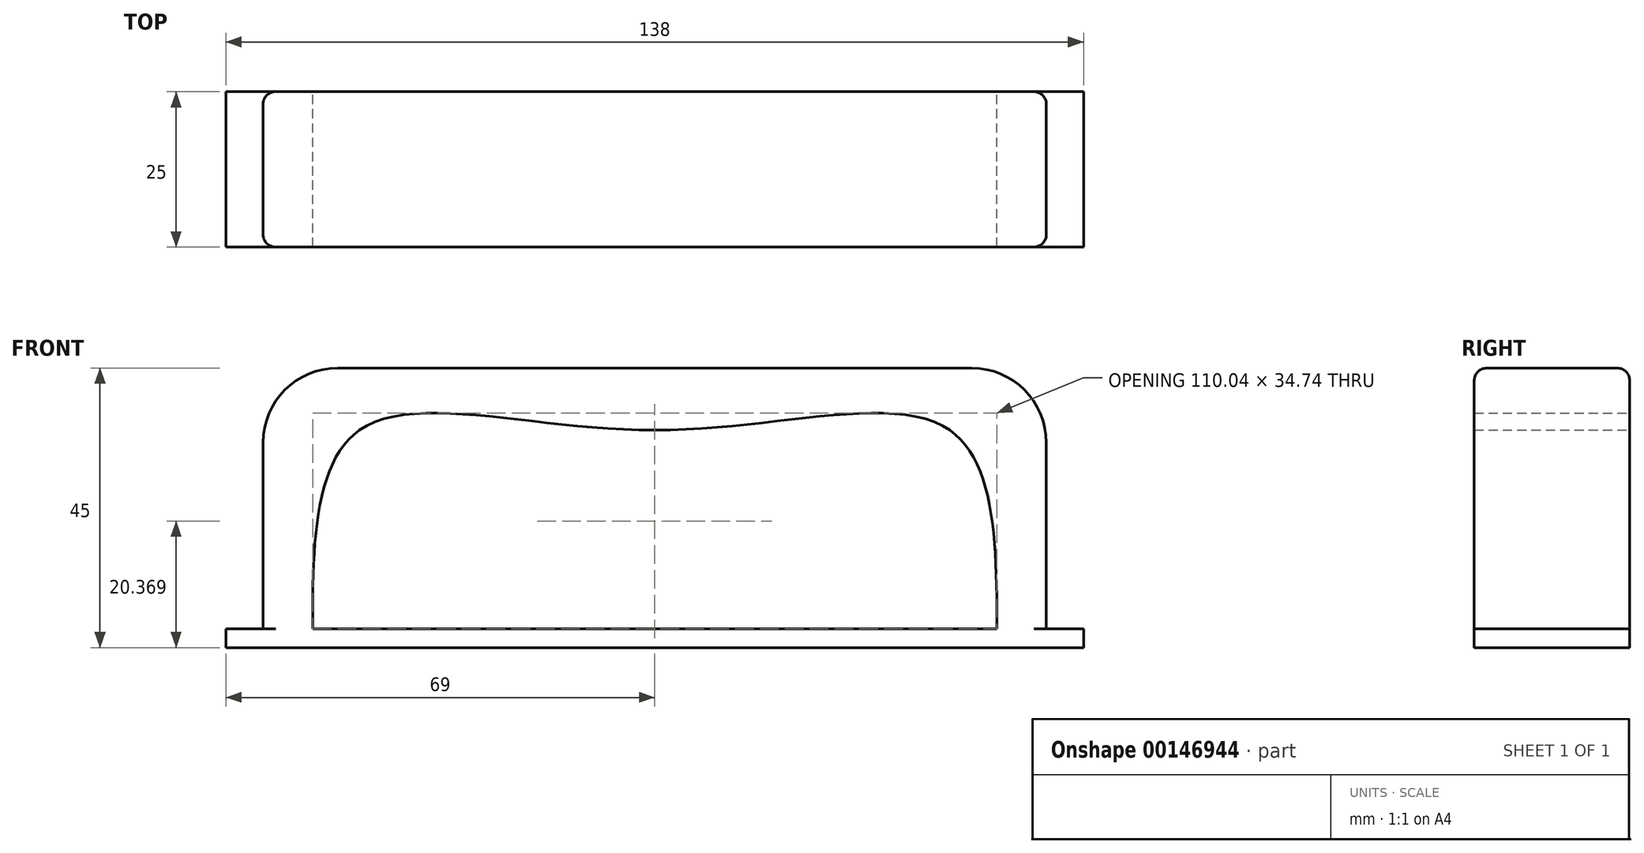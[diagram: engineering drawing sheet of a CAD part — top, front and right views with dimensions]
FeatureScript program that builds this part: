
annotation { "Feature Type Name" : "Feature", "Feature Type Description" : "" }
export const myFeature = defineFeature(function(context is Context, id is Id, definition is map)
    precondition{}
    {
        {
            var Q0;
            Q0=qCreatedBy(makeId("Front.planeOp"),FACE);
            var sketch = newSketch(context, id + "F0", { "sketchPlane" : qUnion([Q0])});
            skLineSegment(sketch, "E0", {"start": v(-55, 0) * mm, "end": v(55, 0) * mm});
            skLineSegment(sketch, "E1", {"start": v(0, 0) * mm, "end": v(0, 35) * mm, "construction": true});
            skLineSegment(sketch, "E2", {"start": v(-47.5, 35) * mm, "end": v(47.5, 35) * mm});
            skFitSpline(sketch, "E3", {"points": [v(-55, 0) * mm, v(-47.5, 35) * mm, v(0, 35) * mm, v(47.5, 35) * mm, v(55, 0) * mm], "startDerivative": vector(-1.45, 191.05) * mm, "endDerivative": vector(-1.45, -191.05) * mm});
            skLineSegment(sketch, "E4", {"start": v(-55, 0) * mm, "end": v(-63, 0) * mm});
            skLineSegment(sketch, "E5", {"start": v(-63, 0) * mm, "end": v(-63, 45) * mm});
            skLineSegment(sketch, "E6", {"start": v(-63, 45) * mm, "end": v(63, 45) * mm});
            skLineSegment(sketch, "E7", {"start": v(63, 45) * mm, "end": v(63, 0) * mm});
            skLineSegment(sketch, "E8", {"start": v(63, 0) * mm, "end": v(55, 0) * mm});
            skLineSegment(sketch, "E9", {"start": v(-63, 0) * mm, "end": v(-69, 0) * mm});
            skLineSegment(sketch, "E10", {"start": v(-69, 0) * mm, "end": v(-69, 3) * mm});
            skLineSegment(sketch, "E11", {"start": v(-69, 3) * mm, "end": v(69, 3) * mm});
            skLineSegment(sketch, "E12", {"start": v(69, 3) * mm, "end": v(69, 0) * mm});
            skLineSegment(sketch, "E13", {"start": v(69, 0) * mm, "end": v(63, 0) * mm});
            skSolve(sketch);
        }
        {
            var Q0;
            Q0 = qSketchRegion(id + "F0", true);
            extrude(context, id + "F1", {"entities" : qUnion([Q0]), "depth" : 25 * mm});
        }
        {
            var Q0;
            Q0=makeQuery(id+"F1.opExtrude","SWEPT_EDGE",EDGE,{"disambiguationData":[OSD([sQuery(id+"F0.wireOp",EDGE,"E5"),sQuery(id+"F0.wireOp",EDGE,"E6")])]});
            var Q1;
            Q1=makeQuery(id+"F1.opExtrude","SWEPT_EDGE",EDGE,{"disambiguationData":[OSD([sQuery(id+"F0.wireOp",EDGE,"E6"),sQuery(id+"F0.wireOp",EDGE,"E7")])]});
            fillet(context, id + "F2", {"entities" : qUnion([Q0, Q1]), "radius" : 12 * mm, "tangentPropagation" : true, "allowEdgeOverflow" : false});
        }
        {
            var Q0;
            Q0=makeQuery(id+"F1.opExtrude","CAP_EDGE",EDGE,{"disambiguationData":[OSD([sQuery(id+"F0.wireOp",EDGE,"E6")])],"isStart":true});
            var Q1;
            {var subQ0=sQuery(id+"F0.wireOp",EDGE,"E6");var subQ1=sQuery(id+"F0.wireOp",EDGE,"E5");Q1=makeQuery(id+"F2.opFillet","BLEND_EDGE",EDGE,{"blendedFrom":[makeQuery(id+"F1.opExtrude","SWEPT_EDGE",EDGE,{"disambiguationData":[OSD([subQ1,subQ0])]}),makeQuery(id+"F1.opExtrude","CAP_FACE",FACE,{"disambiguationData":[OSD([sQuery(id+"F0.wireOp",EDGE,"E0"),sQuery(id+"F0.wireOp",EDGE,"E3"),sQuery(id+"F0.wireOp",EDGE,"E4"),subQ1,subQ0,sQuery(id+"F0.wireOp",EDGE,"E7"),sQuery(id+"F0.wireOp",EDGE,"E8"),sQuery(id+"F0.wireOp",EDGE,"E9"),sQuery(id+"F0.wireOp",EDGE,"E10"),sQuery(id+"F0.wireOp",EDGE,"E11"),sQuery(id+"F0.wireOp",EDGE,"E12"),sQuery(id+"F0.wireOp",EDGE,"E13")])],"isStart":true})],"blendedInto":[makeQuery(id+"F1.opExtrude","CAP_FACE",FACE,{"disambiguationData":[OSD([sQuery(id+"F0.wireOp",EDGE,"E0"),sQuery(id+"F0.wireOp",EDGE,"E3"),sQuery(id+"F0.wireOp",EDGE,"E4"),subQ1,subQ0,sQuery(id+"F0.wireOp",EDGE,"E7"),sQuery(id+"F0.wireOp",EDGE,"E8"),sQuery(id+"F0.wireOp",EDGE,"E9"),sQuery(id+"F0.wireOp",EDGE,"E10"),sQuery(id+"F0.wireOp",EDGE,"E11"),sQuery(id+"F0.wireOp",EDGE,"E12"),sQuery(id+"F0.wireOp",EDGE,"E13")])],"isStart":true})]});}
            var Q2;
            Q2=makeQuery(id+"F1.opExtrude","CAP_EDGE",EDGE,{"disambiguationData":[OSD([sQuery(id+"F0.wireOp",EDGE,"E5")])],"isStart":true});
            var Q3;
            {var subQ0=sQuery(id+"F0.wireOp",EDGE,"E7");var subQ1=sQuery(id+"F0.wireOp",EDGE,"E6");Q3=makeQuery(id+"F2.opFillet","BLEND_EDGE",EDGE,{"blendedFrom":[makeQuery(id+"F1.opExtrude","SWEPT_EDGE",EDGE,{"disambiguationData":[OSD([subQ1,subQ0])]}),makeQuery(id+"F1.opExtrude","CAP_FACE",FACE,{"disambiguationData":[OSD([sQuery(id+"F0.wireOp",EDGE,"E0"),sQuery(id+"F0.wireOp",EDGE,"E3"),sQuery(id+"F0.wireOp",EDGE,"E4"),sQuery(id+"F0.wireOp",EDGE,"E5"),subQ1,subQ0,sQuery(id+"F0.wireOp",EDGE,"E8"),sQuery(id+"F0.wireOp",EDGE,"E9"),sQuery(id+"F0.wireOp",EDGE,"E10"),sQuery(id+"F0.wireOp",EDGE,"E11"),sQuery(id+"F0.wireOp",EDGE,"E12"),sQuery(id+"F0.wireOp",EDGE,"E13")])],"isStart":true})],"blendedInto":[makeQuery(id+"F1.opExtrude","CAP_FACE",FACE,{"disambiguationData":[OSD([sQuery(id+"F0.wireOp",EDGE,"E0"),sQuery(id+"F0.wireOp",EDGE,"E3"),sQuery(id+"F0.wireOp",EDGE,"E4"),sQuery(id+"F0.wireOp",EDGE,"E5"),subQ1,subQ0,sQuery(id+"F0.wireOp",EDGE,"E8"),sQuery(id+"F0.wireOp",EDGE,"E9"),sQuery(id+"F0.wireOp",EDGE,"E10"),sQuery(id+"F0.wireOp",EDGE,"E11"),sQuery(id+"F0.wireOp",EDGE,"E12"),sQuery(id+"F0.wireOp",EDGE,"E13")])],"isStart":true})]});}
            var Q4;
            Q4=makeQuery(id+"F1.opExtrude","CAP_EDGE",EDGE,{"disambiguationData":[OSD([sQuery(id+"F0.wireOp",EDGE,"E7")])],"isStart":true});
            var Q5;
            Q5=makeQuery(id+"F1.opExtrude","CAP_EDGE",EDGE,{"disambiguationData":[OSD([sQuery(id+"F0.wireOp",EDGE,"E5")])],"isStart":false});
            var Q6;
            {var subQ0=sQuery(id+"F0.wireOp",EDGE,"E6");var subQ1=sQuery(id+"F0.wireOp",EDGE,"E5");Q6=makeQuery(id+"F2.opFillet","BLEND_EDGE",EDGE,{"blendedFrom":[makeQuery(id+"F1.opExtrude","SWEPT_EDGE",EDGE,{"disambiguationData":[OSD([subQ1,subQ0])]}),makeQuery(id+"F1.opExtrude","CAP_FACE",FACE,{"disambiguationData":[OSD([sQuery(id+"F0.wireOp",EDGE,"E0"),sQuery(id+"F0.wireOp",EDGE,"E3"),sQuery(id+"F0.wireOp",EDGE,"E4"),subQ1,subQ0,sQuery(id+"F0.wireOp",EDGE,"E7"),sQuery(id+"F0.wireOp",EDGE,"E8"),sQuery(id+"F0.wireOp",EDGE,"E9"),sQuery(id+"F0.wireOp",EDGE,"E10"),sQuery(id+"F0.wireOp",EDGE,"E11"),sQuery(id+"F0.wireOp",EDGE,"E12"),sQuery(id+"F0.wireOp",EDGE,"E13")])],"isStart":false})],"blendedInto":[makeQuery(id+"F1.opExtrude","CAP_FACE",FACE,{"disambiguationData":[OSD([sQuery(id+"F0.wireOp",EDGE,"E0"),sQuery(id+"F0.wireOp",EDGE,"E3"),sQuery(id+"F0.wireOp",EDGE,"E4"),subQ1,subQ0,sQuery(id+"F0.wireOp",EDGE,"E7"),sQuery(id+"F0.wireOp",EDGE,"E8"),sQuery(id+"F0.wireOp",EDGE,"E9"),sQuery(id+"F0.wireOp",EDGE,"E10"),sQuery(id+"F0.wireOp",EDGE,"E11"),sQuery(id+"F0.wireOp",EDGE,"E12"),sQuery(id+"F0.wireOp",EDGE,"E13")])],"isStart":false})]});}
            var Q7;
            Q7=makeQuery(id+"F1.opExtrude","CAP_EDGE",EDGE,{"disambiguationData":[OSD([sQuery(id+"F0.wireOp",EDGE,"E6")])],"isStart":false});
            var Q8;
            {var subQ0=sQuery(id+"F0.wireOp",EDGE,"E7");var subQ1=sQuery(id+"F0.wireOp",EDGE,"E6");Q8=makeQuery(id+"F2.opFillet","BLEND_EDGE",EDGE,{"blendedFrom":[makeQuery(id+"F1.opExtrude","SWEPT_EDGE",EDGE,{"disambiguationData":[OSD([subQ1,subQ0])]}),makeQuery(id+"F1.opExtrude","CAP_FACE",FACE,{"disambiguationData":[OSD([sQuery(id+"F0.wireOp",EDGE,"E0"),sQuery(id+"F0.wireOp",EDGE,"E3"),sQuery(id+"F0.wireOp",EDGE,"E4"),sQuery(id+"F0.wireOp",EDGE,"E5"),subQ1,subQ0,sQuery(id+"F0.wireOp",EDGE,"E8"),sQuery(id+"F0.wireOp",EDGE,"E9"),sQuery(id+"F0.wireOp",EDGE,"E10"),sQuery(id+"F0.wireOp",EDGE,"E11"),sQuery(id+"F0.wireOp",EDGE,"E12"),sQuery(id+"F0.wireOp",EDGE,"E13")])],"isStart":false})],"blendedInto":[makeQuery(id+"F1.opExtrude","CAP_FACE",FACE,{"disambiguationData":[OSD([sQuery(id+"F0.wireOp",EDGE,"E0"),sQuery(id+"F0.wireOp",EDGE,"E3"),sQuery(id+"F0.wireOp",EDGE,"E4"),sQuery(id+"F0.wireOp",EDGE,"E5"),subQ1,subQ0,sQuery(id+"F0.wireOp",EDGE,"E8"),sQuery(id+"F0.wireOp",EDGE,"E9"),sQuery(id+"F0.wireOp",EDGE,"E10"),sQuery(id+"F0.wireOp",EDGE,"E11"),sQuery(id+"F0.wireOp",EDGE,"E12"),sQuery(id+"F0.wireOp",EDGE,"E13")])],"isStart":false})]});}
            var Q9;
            Q9=makeQuery(id+"F1.opExtrude","CAP_EDGE",EDGE,{"disambiguationData":[OSD([sQuery(id+"F0.wireOp",EDGE,"E7")])],"isStart":false});
            fillet(context, id + "F3", {"entities" : qUnion([Q0, Q1, Q2, Q3, Q4, Q5, Q6, Q7, Q8, Q9]), "radius" : 2 * mm, "tangentPropagation" : true, "allowEdgeOverflow" : false});
        }
    });
